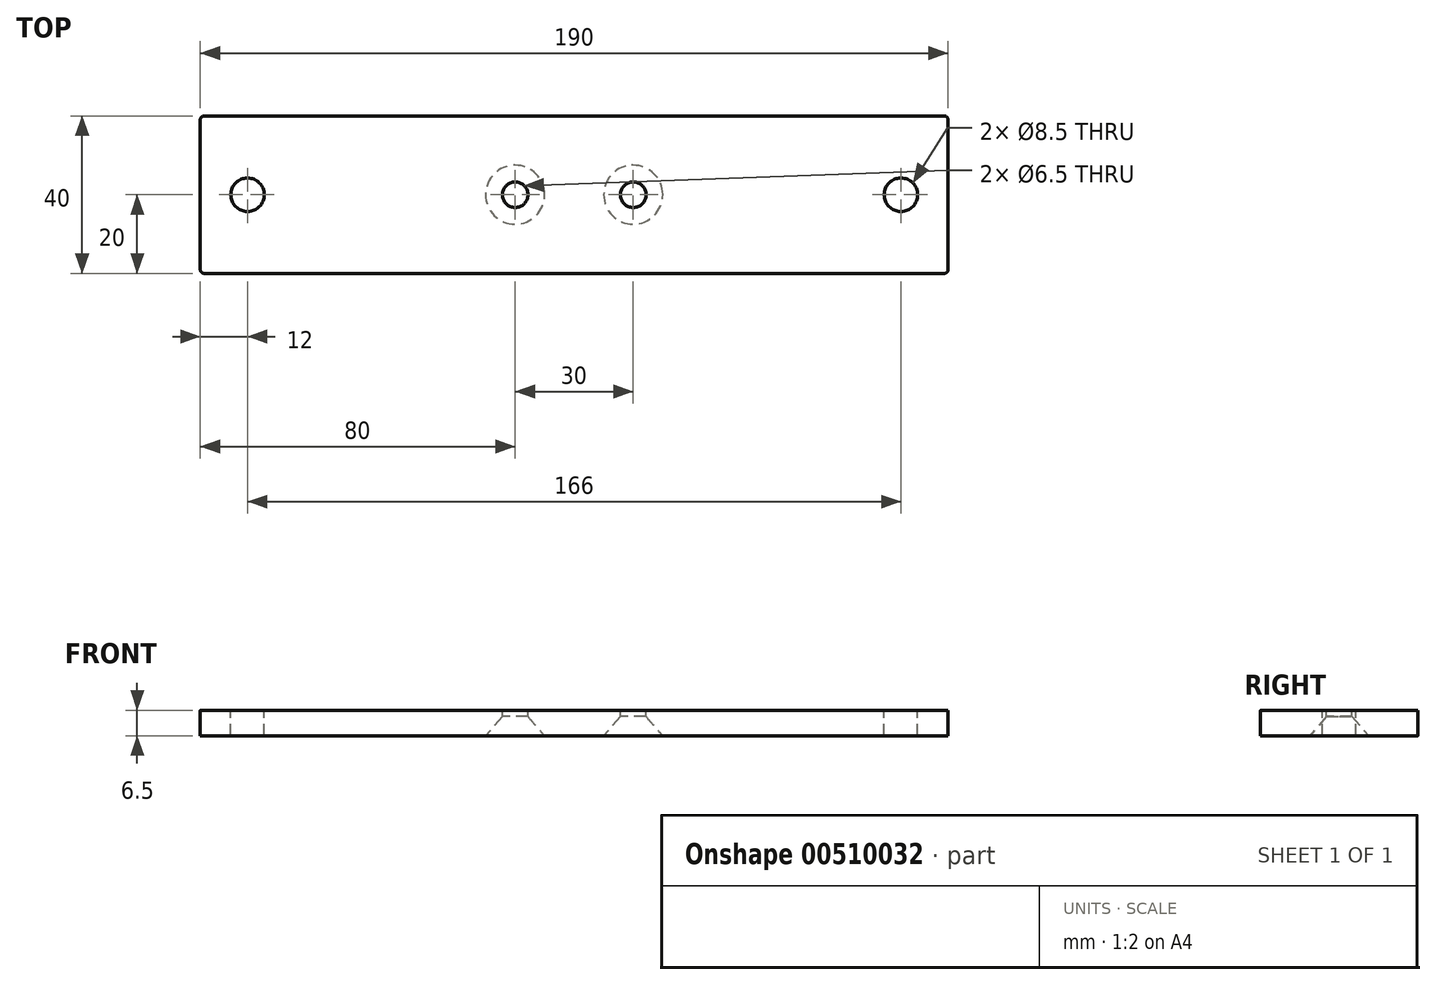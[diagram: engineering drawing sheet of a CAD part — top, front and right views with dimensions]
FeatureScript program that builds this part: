
annotation { "Feature Type Name" : "Feature", "Feature Type Description" : "" }
export const myFeature = defineFeature(function(context is Context, id is Id, definition is map)
    precondition{}
    {
        {
            var Q0;
            Q0=qCreatedBy(makeId("Top.planeOp"),FACE);
            var sketch = newSketch(context, id + "F0", { "sketchPlane" : qUnion([Q0])});
            skLineSegment(sketch, "E0.bottom", {"start": v(-94, 20) * mm, "end": v(94, 20) * mm});
            skLineSegment(sketch, "E0.top", {"start": v(-94, -20) * mm, "end": v(94, -20) * mm});
            skLineSegment(sketch, "E0.left", {"start": v(-95, 19) * mm, "end": v(-95, -19) * mm});
            skLineSegment(sketch, "E0.right", {"start": v(95, 19) * mm, "end": v(95, -19) * mm});
            skPoint(sketch, "E0.middle", {"position": v(0, 0) * mm});
            skPoint(sketch, "E1.visualSharp", {"position": v(-95, 20) * mm});
            skArc(sketch, "E1.filletArc", {"start": v(-94, 20) * mm, "mid": v(-94.7, 19.7) * mm, "end": v(-95, 19) * mm});
            skPoint(sketch, "E2.visualSharp", {"position": v(-95, -20) * mm});
            skArc(sketch, "E2.filletArc", {"start": v(-95, -19) * mm, "mid": v(-94.7, -19.7) * mm, "end": v(-94, -20) * mm});
            skPoint(sketch, "E3.visualSharp", {"position": v(95, 20) * mm});
            skArc(sketch, "E3.filletArc", {"start": v(95, 19) * mm, "mid": v(94.7, 19.7) * mm, "end": v(94, 20) * mm});
            skPoint(sketch, "E4.visualSharp", {"position": v(95, -20) * mm});
            skArc(sketch, "E4.filletArc", {"start": v(94, -20) * mm, "mid": v(94.7, -19.7) * mm, "end": v(95, -19) * mm});
            skPoint(sketch, "E5", {"position": v(-83, 0) * mm});
            skPoint(sketch, "E6", {"position": v(-15, 0) * mm});
            skPoint(sketch, "E7", {"position": v(15, 0) * mm});
            skPoint(sketch, "E8", {"position": v(83, 0) * mm});
            skSolve(sketch);
        }
        {
            var Q0;
            Q0=makeQuery(id+"F0.imprint","IMPRINT",FACE,{"disambiguationData":[TD([[makeQuery(id+"F0.imprint","IMPRINT",EDGE,{"derivedFrom":sQuery(id+"F0.wireOp",EDGE,"E0.bottom")}),-1.0]])]});
            extrude(context, id + "F1", {"entities" : qUnion([Q0]), "depth" : 6.5 * mm});
        }
        {
            var Q0;
            Q0=sQuery(id+"F0.wireOp",VERTEX,"E8");
            var Q1;
            Q1=makeQuery(id+"F1.opExtrude","SWEPT_BODY",BODY,{"disambiguationData":[OSD([sQuery(id+"F0.wireOp",EDGE,"E0.bottom"),sQuery(id+"F0.wireOp",EDGE,"E0.top"),sQuery(id+"F0.wireOp",EDGE,"E0.left"),sQuery(id+"F0.wireOp",EDGE,"E0.right"),sQuery(id+"F0.wireOp",EDGE,"E1.filletArc"),sQuery(id+"F0.wireOp",EDGE,"E2.filletArc"),sQuery(id+"F0.wireOp",EDGE,"E3.filletArc"),sQuery(id+"F0.wireOp",EDGE,"E4.filletArc")])]});
            hole(context, id + "F2", {"style" : HoleStyle.SIMPLE, "endStyle" : HoleEndStyle.THROUGH, "oppositeDirection" : true, "holeDiameter" : 8.5 * mm, "isTappedThrough" : true, "tappedDepth" : 12 * mm, "tapClearance" : 3, "locations" : qUnion([Q0]), "scope" : qUnion([Q1]), "startStyle" : HoleStartStyle.PART});
        }
        {
            var Q0;
            Q0=sQuery(id+"F0.wireOp",VERTEX,"E5");
            var Q1;
            Q1=makeQuery(id+"F1.opExtrude","SWEPT_BODY",BODY,{"disambiguationData":[OSD([sQuery(id+"F0.wireOp",EDGE,"E0.bottom"),sQuery(id+"F0.wireOp",EDGE,"E0.top"),sQuery(id+"F0.wireOp",EDGE,"E0.left"),sQuery(id+"F0.wireOp",EDGE,"E0.right"),sQuery(id+"F0.wireOp",EDGE,"E1.filletArc"),sQuery(id+"F0.wireOp",EDGE,"E2.filletArc"),sQuery(id+"F0.wireOp",EDGE,"E3.filletArc"),sQuery(id+"F0.wireOp",EDGE,"E4.filletArc")])]});
            hole(context, id + "F3", {"style" : HoleStyle.SIMPLE, "endStyle" : HoleEndStyle.THROUGH, "oppositeDirection" : true, "holeDiameter" : 8.5 * mm, "isTappedThrough" : true, "tappedDepth" : 12 * mm, "tapClearance" : 3, "locations" : qUnion([Q0]), "scope" : qUnion([Q1]), "startStyle" : HoleStartStyle.PART});
        }
        {
            var Q0;
            Q0=sQuery(id+"F0.wireOp",VERTEX,"E7");
            var Q1;
            Q1=makeQuery(id+"F1.opExtrude","SWEPT_BODY",BODY,{"disambiguationData":[OSD([sQuery(id+"F0.wireOp",EDGE,"E0.bottom"),sQuery(id+"F0.wireOp",EDGE,"E0.top"),sQuery(id+"F0.wireOp",EDGE,"E0.left"),sQuery(id+"F0.wireOp",EDGE,"E0.right"),sQuery(id+"F0.wireOp",EDGE,"E1.filletArc"),sQuery(id+"F0.wireOp",EDGE,"E2.filletArc"),sQuery(id+"F0.wireOp",EDGE,"E3.filletArc"),sQuery(id+"F0.wireOp",EDGE,"E4.filletArc")])]});
            hole(context, id + "F4", {"style" : HoleStyle.C_SINK, "endStyle" : HoleEndStyle.THROUGH, "oppositeDirection" : true, "holeDiameter" : 6.5 * mm, "cSinkDiameter" : 15 * mm, "cSinkAngle" : 82 * degree, "isTappedThrough" : true, "tappedDepth" : 12 * mm, "tapClearance" : 3, "locations" : qUnion([Q0]), "scope" : qUnion([Q1]), "startStyle" : HoleStartStyle.PART});
        }
        {
            var Q0;
            Q0=sQuery(id+"F0.wireOp",VERTEX,"E6");
            var Q1;
            Q1=makeQuery(id+"F1.opExtrude","SWEPT_BODY",BODY,{"disambiguationData":[OSD([sQuery(id+"F0.wireOp",EDGE,"E0.bottom"),sQuery(id+"F0.wireOp",EDGE,"E0.top"),sQuery(id+"F0.wireOp",EDGE,"E0.left"),sQuery(id+"F0.wireOp",EDGE,"E0.right"),sQuery(id+"F0.wireOp",EDGE,"E1.filletArc"),sQuery(id+"F0.wireOp",EDGE,"E2.filletArc"),sQuery(id+"F0.wireOp",EDGE,"E3.filletArc"),sQuery(id+"F0.wireOp",EDGE,"E4.filletArc")])]});
            hole(context, id + "F5", {"style" : HoleStyle.C_SINK, "endStyle" : HoleEndStyle.THROUGH, "oppositeDirection" : true, "holeDiameter" : 6.5 * mm, "cSinkDiameter" : 15 * mm, "cSinkAngle" : 82 * degree, "isTappedThrough" : true, "tappedDepth" : 12 * mm, "tapClearance" : 3, "locations" : qUnion([Q0]), "scope" : qUnion([Q1]), "startStyle" : HoleStartStyle.PART});
        }
    });
